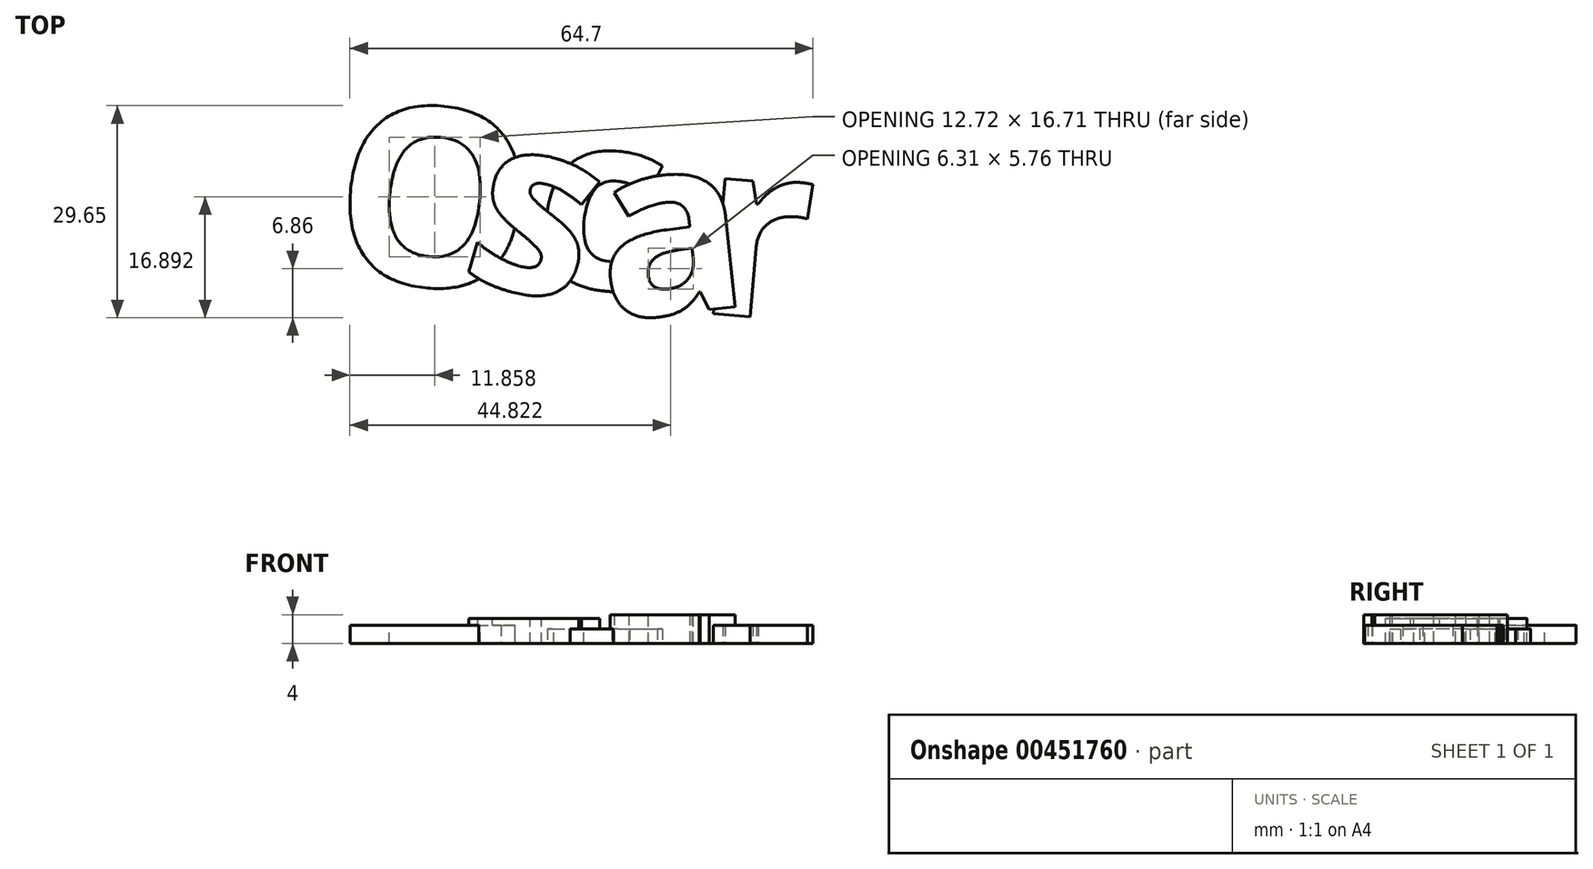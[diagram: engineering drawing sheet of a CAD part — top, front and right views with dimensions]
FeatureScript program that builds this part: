
annotation { "Feature Type Name" : "Feature", "Feature Type Description" : "" }
export const myFeature = defineFeature(function(context is Context, id is Id, definition is map)
    precondition{}
    {
        {
            var Q0;
            Q0=qCreatedBy(makeId("Top.planeOp"),FACE);
            var sketch = newSketch(context, id + "F0", { "sketchPlane" : qUnion([Q0])});
            skText(sketch, "E0", { "text": "O", "fontName": "OpenSans-Bold.ttf"});
            skText(sketch, "E1", { "text": "s", "fontName": "OpenSans-Bold.ttf"});
            skText(sketch, "E2", { "text": "c", "fontName": "OpenSans-Bold.ttf"});
            skText(sketch, "E3", { "text": "a", "fontName": "OpenSans-Bold.ttf"});
            skText(sketch, "E4", { "text": "r", "fontName": "OpenSans-Bold.ttf"});
            skLineSegment(sketch, "E5", {"start": v(-42.37, 50.34) * mm, "end": v(-72.31, 9.01) * mm, "construction": true});
            skLineSegment(sketch, "E6", {"start": v(-42.37, 50.34) * mm, "end": v(-72.98, 50.34) * mm, "construction": true});
            const initialGuessF0  = {"E0": [-0.0505, -0.01028, 0.99466, -0.10322, 0.025], "E1": [-0.03246, -0.01007, 0.96162, -0.27437, 0.025], "E2": [-0.0225, -0.01084, 0.99255, -0.12187, 0.025], "E3": [-0.01178, -0.0166, 0.99452, 0.10453, 0.025], "E4": [0.00072, -0.0154, 0.9962, -0.08716, 0.025]};
            skSetInitialGuess(sketch, initialGuessF0);
            skSolve(sketch);
        }
        {
            var Q0;
            {var subQ12=sQuery(id+"F0.wireOp",EDGE,"E0.sketch_text.stroke-1");Q0=makeQuery(id+"F0.imprint","IMPRINT",FACE,{"disambiguationData":[TD([[makeQuery(id+"F0.imprint","IMPRINT",EDGE,{"derivedFrom":subQ12}),-1.0]])]});}
            var Q1;
            {var subQ9=sQuery(id+"F0.wireOp",EDGE,"E1.sketch_text.stroke-12");Q1=makeQuery(id+"F0.imprint","IMPRINT",FACE,{"disambiguationData":[TD([[makeQuery(id+"F0.imprint","IMPRINT",EDGE,{"derivedFrom":subQ9}),-1.0]])]});}
            var Q2;
            {var subQ12=sQuery(id+"F0.wireOp",EDGE,"E0.sketch_text.stroke-2");Q2=makeQuery(id+"F0.imprint","IMPRINT",FACE,{"disambiguationData":[TD([[makeQuery(id+"F0.imprint","IMPRINT",EDGE,{"derivedFrom":subQ12}),-1.0]])]});}
            extrude(context, id + "F1", {"entities" : qUnion([Q0, Q1, Q2]), "depth" : 2.5 * mm, "offsetDistance" : 25 * mm});
        }
        {
            var Q0;
            {var subQ9=sQuery(id+"F0.wireOp",EDGE,"E1.sketch_text.stroke-19");Q0=makeQuery(id+"F0.imprint","IMPRINT",FACE,{"disambiguationData":[TD([[makeQuery(id+"F0.imprint","IMPRINT",EDGE,{"derivedFrom":subQ9}),-1.0]])]});}
            var Q1;
            {var subQ5=sQuery(id+"F0.wireOp",EDGE,"E1.sketch_text.stroke-17");Q1=makeQuery(id+"F0.imprint","IMPRINT",FACE,{"disambiguationData":[TD([[makeQuery(id+"F0.imprint","IMPRINT",EDGE,{"derivedFrom":subQ5}),-1.0]])]});}
            var Q2;
            {var subQ0=sQuery(id+"F0.wireOp",EDGE,"E1.sketch_text.stroke-14");Q2=makeQuery(id+"F0.imprint","IMPRINT",FACE,{"disambiguationData":[TD([[makeQuery(id+"F0.imprint","IMPRINT",EDGE,{"derivedFrom":subQ0}),-1.0]])]});}
            var Q3;
            {var subQ9=sQuery(id+"F0.wireOp",EDGE,"E1.sketch_text.stroke-12");Q3=makeQuery(id+"F0.imprint","IMPRINT",FACE,{"disambiguationData":[TD([[makeQuery(id+"F0.imprint","IMPRINT",EDGE,{"derivedFrom":subQ9}),-1.0]])]});}
            var Q4;
            {var subQ9=sQuery(id+"F0.wireOp",EDGE,"E1.sketch_text.stroke-1");Q4=makeQuery(id+"F0.imprint","IMPRINT",FACE,{"disambiguationData":[TD([[makeQuery(id+"F0.imprint","IMPRINT",EDGE,{"derivedFrom":subQ9}),-1.0]])]});}
            var Q5;
            {var subQ0=sQuery(id+"F0.wireOp",EDGE,"E1.sketch_text.stroke-24");Q5=makeQuery(id+"F0.imprint","IMPRINT",FACE,{"disambiguationData":[TD([[makeQuery(id+"F0.imprint","IMPRINT",EDGE,{"derivedFrom":subQ0}),-1.0]])]});}
            var Q6;
            {var subQ0=sQuery(id+"F0.wireOp",EDGE,"E1.sketch_text.stroke-4");Q6=makeQuery(id+"F0.imprint","IMPRINT",FACE,{"disambiguationData":[TD([[makeQuery(id+"F0.imprint","IMPRINT",EDGE,{"derivedFrom":subQ0}),-1.0]])]});}
            extrude(context, id + "F2", {"entities" : qUnion([Q0, Q1, Q2, Q3, Q4, Q5, Q6]), "operationType" : NewBodyOperationType.ADD, "depth" : 3.5 * mm, "offsetDistance" : 25 * mm});
        }
        {
            var Q0;
            {var subQ0=sQuery(id+"F0.wireOp",EDGE,"E2.sketch_text.stroke-5");Q0=makeQuery(id+"F0.imprint","IMPRINT",FACE,{"disambiguationData":[TD([[makeQuery(id+"F0.imprint","IMPRINT",EDGE,{"derivedFrom":subQ0}),-1.0]])]});}
            var Q1;
            {var subQ19=sQuery(id+"F0.wireOp",EDGE,"E1.sketch_text.stroke-17");Q1=makeQuery(id+"F0.imprint","IMPRINT",FACE,{"disambiguationData":[TD([[makeQuery(id+"F0.imprint","IMPRINT",EDGE,{"derivedFrom":subQ19}),1.0]])]});}
            var Q2;
            {var subQ5=sQuery(id+"F0.wireOp",EDGE,"E1.sketch_text.stroke-17");Q2=makeQuery(id+"F0.imprint","IMPRINT",FACE,{"disambiguationData":[TD([[makeQuery(id+"F0.imprint","IMPRINT",EDGE,{"derivedFrom":subQ5}),-1.0]])]});}
            var Q3;
            {var subQ0=sQuery(id+"F0.wireOp",EDGE,"E1.sketch_text.stroke-24");Q3=makeQuery(id+"F0.imprint","IMPRINT",FACE,{"disambiguationData":[TD([[makeQuery(id+"F0.imprint","IMPRINT",EDGE,{"derivedFrom":subQ0}),-1.0]])]});}
            var Q4;
            {var subQ6=sQuery(id+"F0.wireOp",EDGE,"E2.sketch_text.stroke-10");Q4=makeQuery(id+"F0.imprint","IMPRINT",FACE,{"disambiguationData":[TD([[makeQuery(id+"F0.imprint","IMPRINT",EDGE,{"derivedFrom":subQ6}),-1.0]])]});}
            extrude(context, id + "F3", {"entities" : qUnion([Q0, Q1, Q2, Q3, Q4]), "operationType" : NewBodyOperationType.ADD, "depth" : 2 * mm, "offsetDistance" : 25 * mm});
        }
        {
            var Q0;
            {var subQ0=sQuery(id+"F0.wireOp",EDGE,"E2.sketch_text.stroke-5");Q0=makeQuery(id+"F0.imprint","IMPRINT",FACE,{"disambiguationData":[TD([[makeQuery(id+"F0.imprint","IMPRINT",EDGE,{"derivedFrom":subQ0}),-1.0]])]});}
            var Q1;
            {var subQ13=sQuery(id+"F0.wireOp",EDGE,"E2.sketch_text.stroke-5");Q1=makeQuery(id+"F0.imprint","IMPRINT",FACE,{"disambiguationData":[TD([[makeQuery(id+"F0.imprint","IMPRINT",EDGE,{"derivedFrom":subQ13}),1.0]])]});}
            var Q2;
            {var subQ6=sQuery(id+"F0.wireOp",EDGE,"E2.sketch_text.stroke-10");Q2=makeQuery(id+"F0.imprint","IMPRINT",FACE,{"disambiguationData":[TD([[makeQuery(id+"F0.imprint","IMPRINT",EDGE,{"derivedFrom":subQ6}),-1.0]])]});}
            var Q3;
            {var subQ0=sQuery(id+"F0.wireOp",EDGE,"E3.sketch_text.stroke-16");Q3=makeQuery(id+"F0.imprint","IMPRINT",FACE,{"disambiguationData":[TD([[makeQuery(id+"F0.imprint","IMPRINT",EDGE,{"derivedFrom":subQ0}),-1.0]])]});}
            extrude(context, id + "F4", {"entities" : qUnion([Q0, Q1, Q2, Q3]), "operationType" : NewBodyOperationType.ADD, "depth" : 4 * mm, "offsetDistance" : 25 * mm});
        }
        {
            var Q0;
            {var subQ0=sQuery(id+"F0.wireOp",EDGE,"E3.sketch_text.stroke-16");Q0=makeQuery(id+"F0.imprint","IMPRINT",FACE,{"disambiguationData":[TD([[makeQuery(id+"F0.imprint","IMPRINT",EDGE,{"derivedFrom":subQ0}),-1.0]])]});}
            var Q1;
            {var subQ1=sQuery(id+"F0.wireOp",EDGE,"E3.sketch_text.stroke-16");Q1=makeQuery(id+"F0.imprint","IMPRINT",FACE,{"disambiguationData":[TD([[makeQuery(id+"F0.imprint","IMPRINT",EDGE,{"derivedFrom":subQ1}),1.0]])]});}
            extrude(context, id + "F5", {"entities" : qUnion([Q0, Q1]), "operationType" : NewBodyOperationType.ADD, "depth" : 2.5 * mm, "offsetDistance" : 25 * mm});
        }
    });
